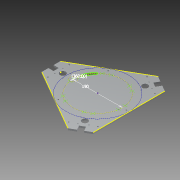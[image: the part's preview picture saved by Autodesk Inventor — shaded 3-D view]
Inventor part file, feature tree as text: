
AUTODESK INVENTOR PART (.ipt)
format: ipt  version: 2015 SP1 (Build 190203100, 203)  size: 219,648 bytes
history: native  units: mm
features: sketch x5, reference x5, extrude x3, hole x3
ambient origin geometry x8: Origin, YZ Plane, XZ Plane, XY Plane, X Axis, Y Axis, Z Axis, Center Point
bodies: Solid1 (feature_tree)
feature tree (16):
  extrude  "Extrusion1"  Depth=6.35mm TaperAngle=0.0deg
  hole  "Hole1"  [1 undecoded]
  extrude  "Extrusion2"  Depth=31.0mm
  hole  "Hole2"  [1 undecoded]
  sketch  "Sketch5"  dims[d17=3.4mm d18=6.0mm d19=6.5mm d20=3.0mm d21=90.0deg d22=8.0mm d23=20.594885mm d24=22.5mm d25=30.0mm d27=360.0deg d29=0.0mm d30=0.0mm d31=20.0mm d32=20.0mm d33=30.0mm d35=360.0deg d37=4.5mm d38=6.0mm d39=8.0mm d40=4.0mm d41=90.0deg d42=8.0mm d43=20.594885mm d45=190.0mm d46=25.0mm d47=60.0mm d49=360.0deg d51=10.0mm d52=0.0mm d53=3.4mm d54=6.0mm d55=6.5mm d56=3.0mm d57=90.0deg d58=8.0mm d59=20.594885mm]
  extrude  "Extrusion3"  Depth=10.0mm
  hole  "Hole3"  [1 undecoded]
  sketch  "Sketch1"  dims[d0=20.0mm d1=20.0mm d2=20.0mm d3=20.0mm d4=20.0mm d5=20.0mm d6=6.35mm d7=0.0mm]
  sketch  "Sketch2"  dims[d8=180.0mm d9=42.5mm]
  reference  "Reference1"
  reference  "Reference2"
  reference  "Reference3"
  sketch  "Sketch3"  dims[d10=42.5mm d11=31.0mm]
  sketch  "Sketch4"  dims[d12=31.0mm d13=30.0mm d15=360.0deg]
  reference  "Reference4"
  reference  "Reference5"
note: 3 required parameter values undecoded (feature->parameter linkage not recoverable at this tier; creation-order binding heuristic only, values carry confidence <= 0.55)
